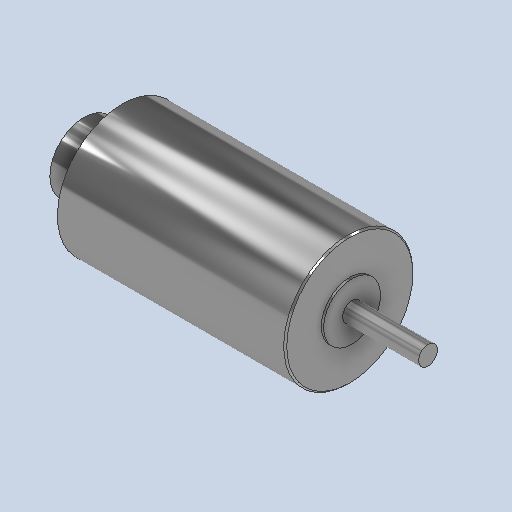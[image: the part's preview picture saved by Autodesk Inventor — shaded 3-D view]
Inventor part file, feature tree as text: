
AUTODESK INVENTOR PART (.ipt)
format: ipt  version: 2025 (Build 290162000, 162)  size: 139,264 bytes
history: native  units: in
note: dims shown in document units (in); Inventor stores cm internally (conversion verified against a paired STEP export)
features: other x3, sketch x3
ambient origin geometry x8: Origin, YZ Plane, XZ Plane, XY Plane, X Axis, Y Axis, Z Axis, Center Point
bodies: Solid1 (feature_tree)
feature tree (6):
  other  "silniczek.ipt"
  other  "Solid1::silniczek.ipt"
  other  "TaggingFeature1"
  sketch  "Sketch1"  dims[d0=0.3937in]
  sketch  "Sketch4"
  sketch  "Sketch5"
